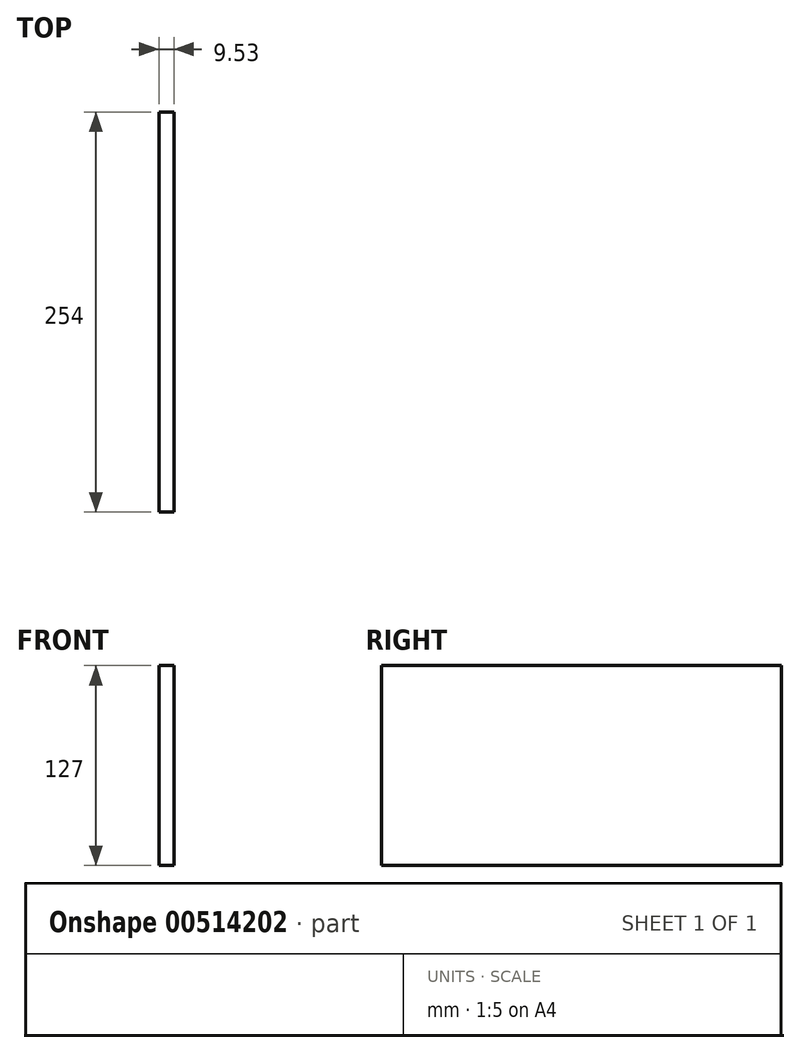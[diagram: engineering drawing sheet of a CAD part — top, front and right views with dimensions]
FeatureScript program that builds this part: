
annotation { "Feature Type Name" : "Feature", "Feature Type Description" : "" }
export const myFeature = defineFeature(function(context is Context, id is Id, definition is map)
    precondition{}
    {
        {
            var Q0;
            Q0=qCreatedBy(makeId("Right.planeOp"),FACE);
            var sketch = newSketch(context, id + "F0", { "sketchPlane" : qUnion([Q0])});
            skLineSegment(sketch, "E0.bottom", {"start": v(-52, 127) * mm, "end": v(202, 127) * mm});
            skLineSegment(sketch, "E0.top", {"start": v(-52, 0) * mm, "end": v(202, 0) * mm});
            skLineSegment(sketch, "E0.left", {"start": v(-52, 127) * mm, "end": v(-52, 0) * mm});
            skLineSegment(sketch, "E0.right", {"start": v(202, 127) * mm, "end": v(202, 0) * mm});
            skSolve(sketch);
        }
        {
            var Q0;
            Q0 = qSketchRegion(id + "F0", true);
            extrude(context, id + "F1", {"entities" : qUnion([Q0]), "depth" : 9.52 * mm, "offsetDistance" : 25.4 * mm});
        }
    });
